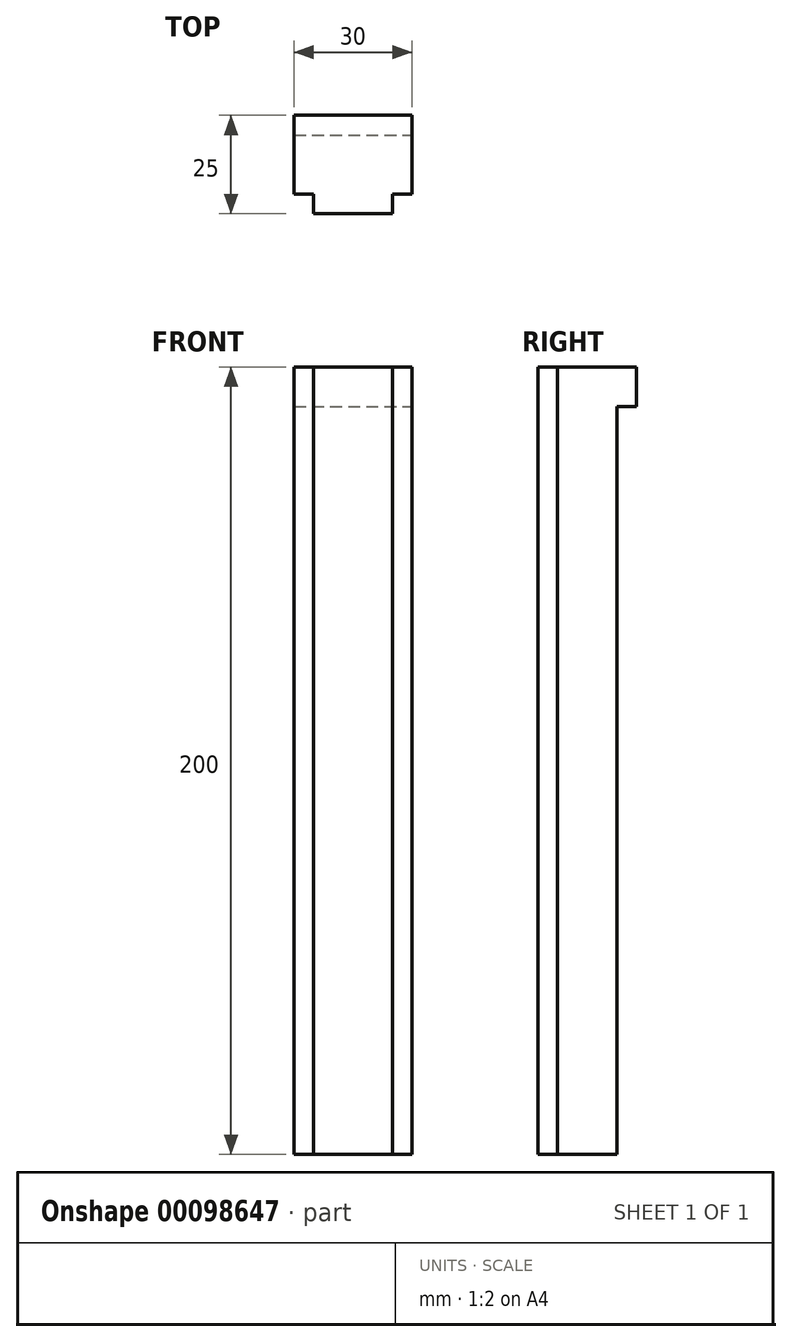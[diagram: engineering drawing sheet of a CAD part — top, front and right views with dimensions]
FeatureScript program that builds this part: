
annotation { "Feature Type Name" : "Feature", "Feature Type Description" : "" }
export const myFeature = defineFeature(function(context is Context, id is Id, definition is map)
    precondition{}
    {
        {
            var Q0;
            Q0=qCreatedBy(makeId("Top.planeOp"),FACE);
            var sketch = newSketch(context, id + "F0", { "sketchPlane" : qUnion([Q0])});
            skLineSegment(sketch, "E0.bottom", {"start": v(15, 7.5) * mm, "end": v(-15, 7.5) * mm});
            skLineSegment(sketch, "E0.top", {"start": v(15, -7.5) * mm, "end": v(-15, -7.5) * mm});
            skLineSegment(sketch, "E0.left", {"start": v(15, 7.5) * mm, "end": v(15, -7.5) * mm});
            skLineSegment(sketch, "E0.right", {"start": v(-15, 7.5) * mm, "end": v(-15, -7.5) * mm});
            skPoint(sketch, "E0.middle", {"position": v(0, 0) * mm});
            skLineSegment(sketch, "E1.bottom", {"start": v(-10, -12.5) * mm, "end": v(10, -12.5) * mm});
            skLineSegment(sketch, "E1.top", {"start": v(-10, -2.5) * mm, "end": v(10, -2.5) * mm});
            skLineSegment(sketch, "E1.left", {"start": v(-10, -12.5) * mm, "end": v(-10, -2.5) * mm});
            skLineSegment(sketch, "E1.right", {"start": v(10, -12.5) * mm, "end": v(10, -2.5) * mm});
            skPoint(sketch, "E1.middle", {"position": v(0, -7.5) * mm});
            skSolve(sketch);
        }
        {
            var Q0;
            Q0=makeQuery(id+"F0.imprint","IMPRINT",FACE,{"disambiguationData":[TD([[makeQuery(id+"F0.imprint","IMPRINT",EDGE,{"derivedFrom":sQuery(id+"F0.wireOp",EDGE,"E0.bottom")}),1.0]])]});
            var Q1;
            {var subQ5=sQuery(id+"F0.wireOp",EDGE,"E1.top");Q1=makeQuery(id+"F0.imprint","IMPRINT",FACE,{"disambiguationData":[TD([[makeQuery(id+"F0.imprint","IMPRINT",EDGE,{"derivedFrom":subQ5}),-1.0]])]});}
            var Q2;
            {var subQ5=sQuery(id+"F0.wireOp",EDGE,"E1.bottom");Q2=makeQuery(id+"F0.imprint","IMPRINT",FACE,{"disambiguationData":[TD([[makeQuery(id+"F0.imprint","IMPRINT",EDGE,{"derivedFrom":subQ5}),1.0]])]});}
            extrude(context, id + "F1", {"entities" : qUnion([Q0, Q1, Q2]), "depth" : 200 * mm});
        }
        {
            var Q0;
            Q0=makeQuery(id+"F1.opExtrude","SWEPT_FACE",FACE,{"disambiguationData":[OSD([sQuery(id+"F0.wireOp",EDGE,"E0.bottom")])]});
            var sketch = newSketch(context, id + "F2", { "sketchPlane" : qUnion([Q0])});
            skLineSegment(sketch, "E2.bottom", {"start": v(15, 200) * mm, "end": v(-15, 200) * mm});
            skLineSegment(sketch, "E2.top", {"start": v(15, 190) * mm, "end": v(-15, 190) * mm});
            skLineSegment(sketch, "E2.left", {"start": v(15, 200) * mm, "end": v(15, 190) * mm});
            skLineSegment(sketch, "E2.right", {"start": v(-15, 200) * mm, "end": v(-15, 190) * mm});
            skSolve(sketch);
        }
        {
            var Q0;
            Q0=makeQuery(id+"F2.imprint","IMPRINT",FACE,{"disambiguationData":[TD([[makeQuery(id+"F2.imprint","IMPRINT",EDGE,{"derivedFrom":sQuery(id+"F2.wireOp",EDGE,"E2.bottom")}),-1.0]])]});
            extrude(context, id + "F3", {"entities" : qUnion([Q0]), "operationType" : NewBodyOperationType.ADD, "depth" : 5 * mm});
        }
    });
